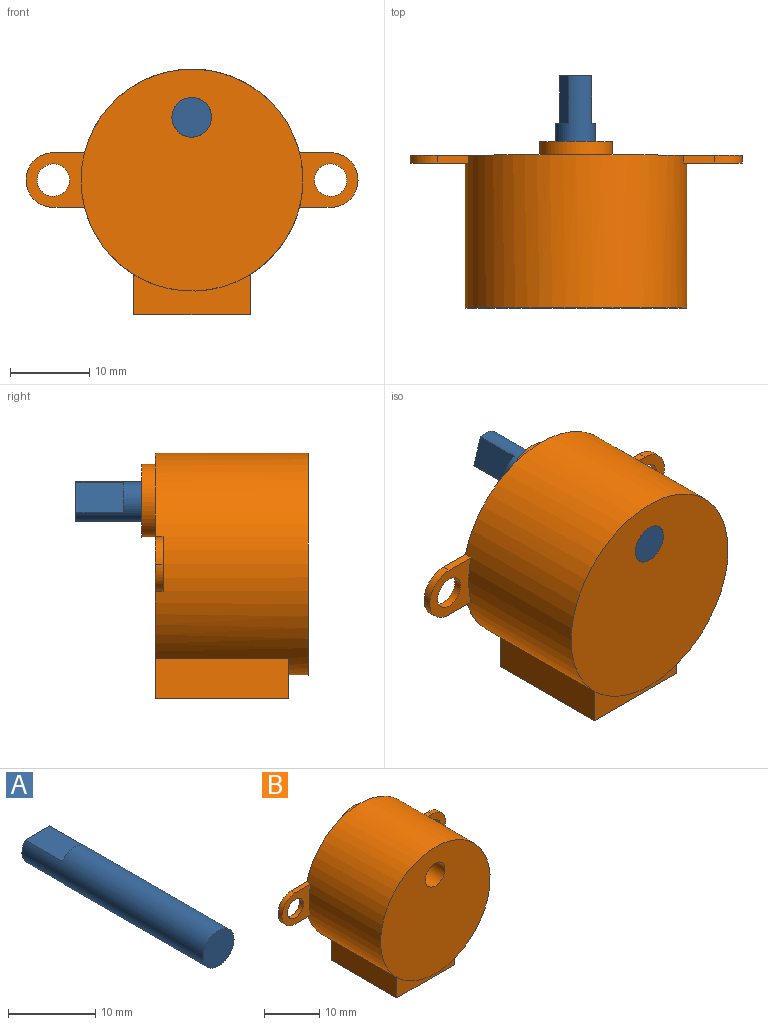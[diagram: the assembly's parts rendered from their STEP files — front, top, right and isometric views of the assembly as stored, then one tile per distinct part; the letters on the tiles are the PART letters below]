
ASSEMBLY  parts=2 mates=1
PART A: 7 faces, bbox 5x29.3x5 mm
  f0: cylinder r=2.5mm len=29.3mm, axis (0,-1,0), area 404.6mm2, adj f1,f2,f3,f4,f5,f6
  f1: plane 4x1mm, normal (0,1,0), area 2.8mm2, adj f0,f4
  f2: plane 5x5mm, normal (0,-1,0), area 19.6mm2, adj f0
  f3: plane 6x4mm, normal (0,0,1), area 24mm2, adj f0,f5,f6
  f4: plane 6x4mm, normal (0,0,-1), area 24mm2, adj f0,f1,f5
  f5: plane 5x3mm, normal (0,1,0), area 14mm2, adj f0,f3,f4
  f6: plane 4x1mm, normal (0,1,0), area 2.8mm2, adj f0,f3
PART B: 22 faces, bbox 41.9x21x31 mm
  f0: cylinder r=14mm len=28mm, axis (0,1,0), area 1423.8mm2, adj f2,f3,f4,f6,f7,f11,f12,f15
  f1: cylinder r=2.5mm len=21mm, axis (0,1,0), area 329.9mm2, adj f2,f9
  f2: plane 28x28mm, normal (0,-1,0), area 596.1mm2, adj f0,f1
  f3: plane 41.9x31mm, normal (0,1,0), area 664.5mm2, adj f0,f4,f5,f6,f8,f10,f11,f12
  f4: plane 16.8x5.08mm, normal (-1,0,0), area 85.4mm2, adj f0,f3,f5,f7
  f5: plane 16.8x14.7mm, normal (0,0,-1), area 247mm2, adj f3,f4,f6,f7
  f6: plane 16.8x5.08mm, normal (1,0,0), area 85.4mm2, adj f0,f3,f5,f7
  f7: plane 14.7x5.08mm, normal (0,-1,0), area 54mm2, adj f0,f4,f5,f6
  f8: cylinder r=4.6mm len=9.2mm, axis (0,-1,0), area 49.1mm2, adj f3,f9
  f9: plane 9.2x9.2mm, normal (0,1,0), area 46.8mm2, adj f1,f8
  f10: cylinder r=3.45mm len=3.45mm, axis (0,1,0), area 5.4mm2, adj f3,f11,f14,f15
  f11: plane 3.93x1mm, normal (0,0,1), area 3.9mm2, adj f0,f3,f10,f15
  f12: plane 3.98x1mm, normal (0,0,-1), area 4mm2, adj f0,f3,f14,f15
  f13: cylinder r=2.05mm len=4.1mm, axis (0,1,0), area 12.9mm2, adj f3,f15
  f14: cylinder r=3.45mm len=3.45mm, axis (0,1,0), area 5.4mm2, adj f3,f10,f12,f15
  f15: plane 7.38x6.9mm, normal (0,-1,0), area 30.6mm2, adj f0,f10,f11,f12,f13,f14
  f16: plane 3.93x1mm, normal (0,0,1), area 3.9mm2, adj f0,f3,f17,f21
  f17: cylinder r=3.45mm len=3.45mm, axis (0,1,0), area 5.4mm2, adj f3,f16,f18,f21
  f18: cylinder r=3.45mm len=3.45mm, axis (0,1,0), area 5.4mm2, adj f3,f17,f19,f21
  f19: plane 3.98x1mm, normal (0,0,-1), area 4mm2, adj f0,f3,f18,f21
  f20: cylinder r=2.05mm len=4.1mm, axis (0,1,0), area 12.9mm2, adj f3,f21
  f21: plane 7.38x6.9mm, normal (0,-1,0), area 30.6mm2, adj f0,f16,f17,f18,f19,f20
PLACE A rot(axis=(0,1,0),107.1deg) t=(-76.76,-12.15,73.21)mm
PLACE B t=(6.71,7.15,-53.32)mm fixed
MATE revolute A.f0 <-> B.f1  axis (0,-1,0) through (20.88,-12.15,46.81)mm
